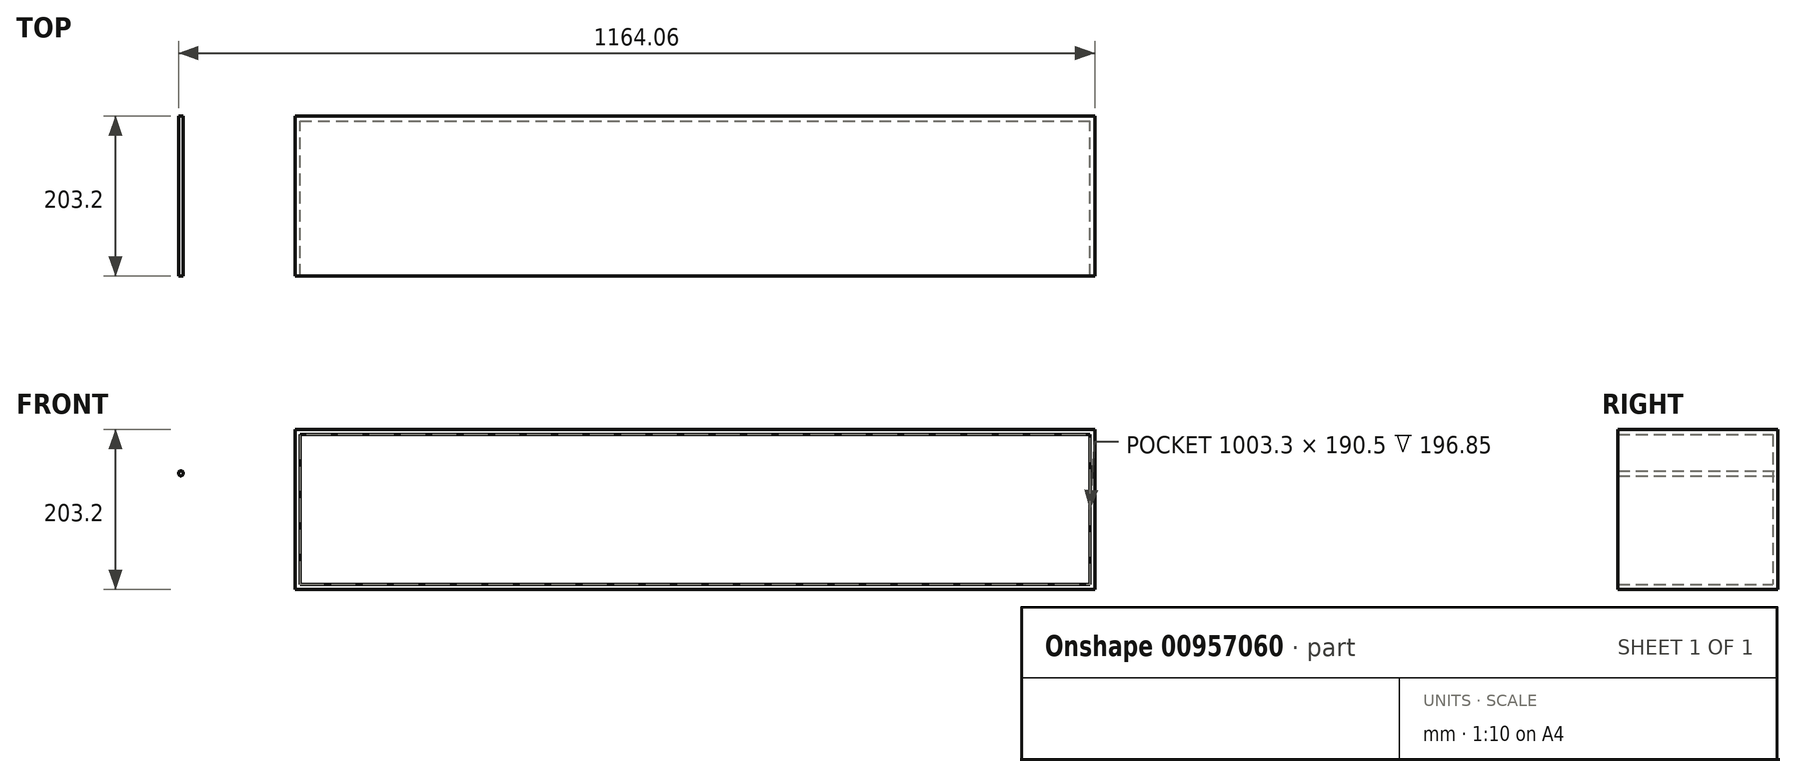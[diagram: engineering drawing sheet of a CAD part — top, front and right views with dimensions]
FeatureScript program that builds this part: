
annotation { "Feature Type Name" : "Feature", "Feature Type Description" : "" }
export const myFeature = defineFeature(function(context is Context, id is Id, definition is map)
    precondition{}
    {
        {
            var Q0;
            Q0=qCreatedBy(makeId("Front.planeOp"),FACE);
            var sketch = newSketch(context, id + "F0", { "sketchPlane" : qUnion([Q0])});
            skLineSegment(sketch, "E0.bottom", {"start": v(-904.81, 109.02) * mm, "end": v(111.19, 109.02) * mm});
            skLineSegment(sketch, "E0.top", {"start": v(-904.81, -94.18) * mm, "end": v(111.19, -94.18) * mm});
            skLineSegment(sketch, "E0.left", {"start": v(-904.81, 109.02) * mm, "end": v(-904.81, -94.18) * mm});
            skLineSegment(sketch, "E0.right", {"start": v(111.19, 109.02) * mm, "end": v(111.19, -94.18) * mm});
            skSolve(sketch);
        }
        {
            var Q0;
            Q0 = qSketchRegion(id + "F0", true);
            extrude(context, id + "F1", {"entities" : qUnion([Q0]), "depth" : 203.2 * mm, "offsetDistance" : 25.4 * mm});
        }
        {
            var Q0;
            Q0=makeQuery(id+"F1.opExtrude","CAP_FACE",FACE,{"disambiguationData":[OSD([sQuery(id+"F0.wireOp",EDGE,"E0.bottom"),sQuery(id+"F0.wireOp",EDGE,"E0.top"),sQuery(id+"F0.wireOp",EDGE,"E0.left"),sQuery(id+"F0.wireOp",EDGE,"E0.right")])],"isStart":false});
            shell(context, id + "F2", {"entities" : qUnion([Q0]), "thickness" : 6.35 * mm});
        }
        {
            var Q0;
            Q0=qCreatedBy(makeId("Front.planeOp"),FACE);
            var sketch = newSketch(context, id + "F3", { "sketchPlane" : qUnion([Q0])});
            skCircle(sketch, "E1", {"center": v(-1049.7, 53.4) * mm, "radius": 3.18 * mm});
            skSolve(sketch);
        }
        {
            var Q0;
            Q0=makeQuery(id+"F3.imprint","IMPRINT",FACE,{"disambiguationData":[TD([[makeQuery(id+"F3.imprint","IMPRINT",EDGE,{"derivedFrom":sQuery(id+"F3.wireOp",EDGE,"E1")}),1.0]])]});
            extrude(context, id + "F4", {"entities" : qUnion([Q0]), "depth" : 203.2 * mm, "offsetDistance" : 25.4 * mm});
        }
    });
